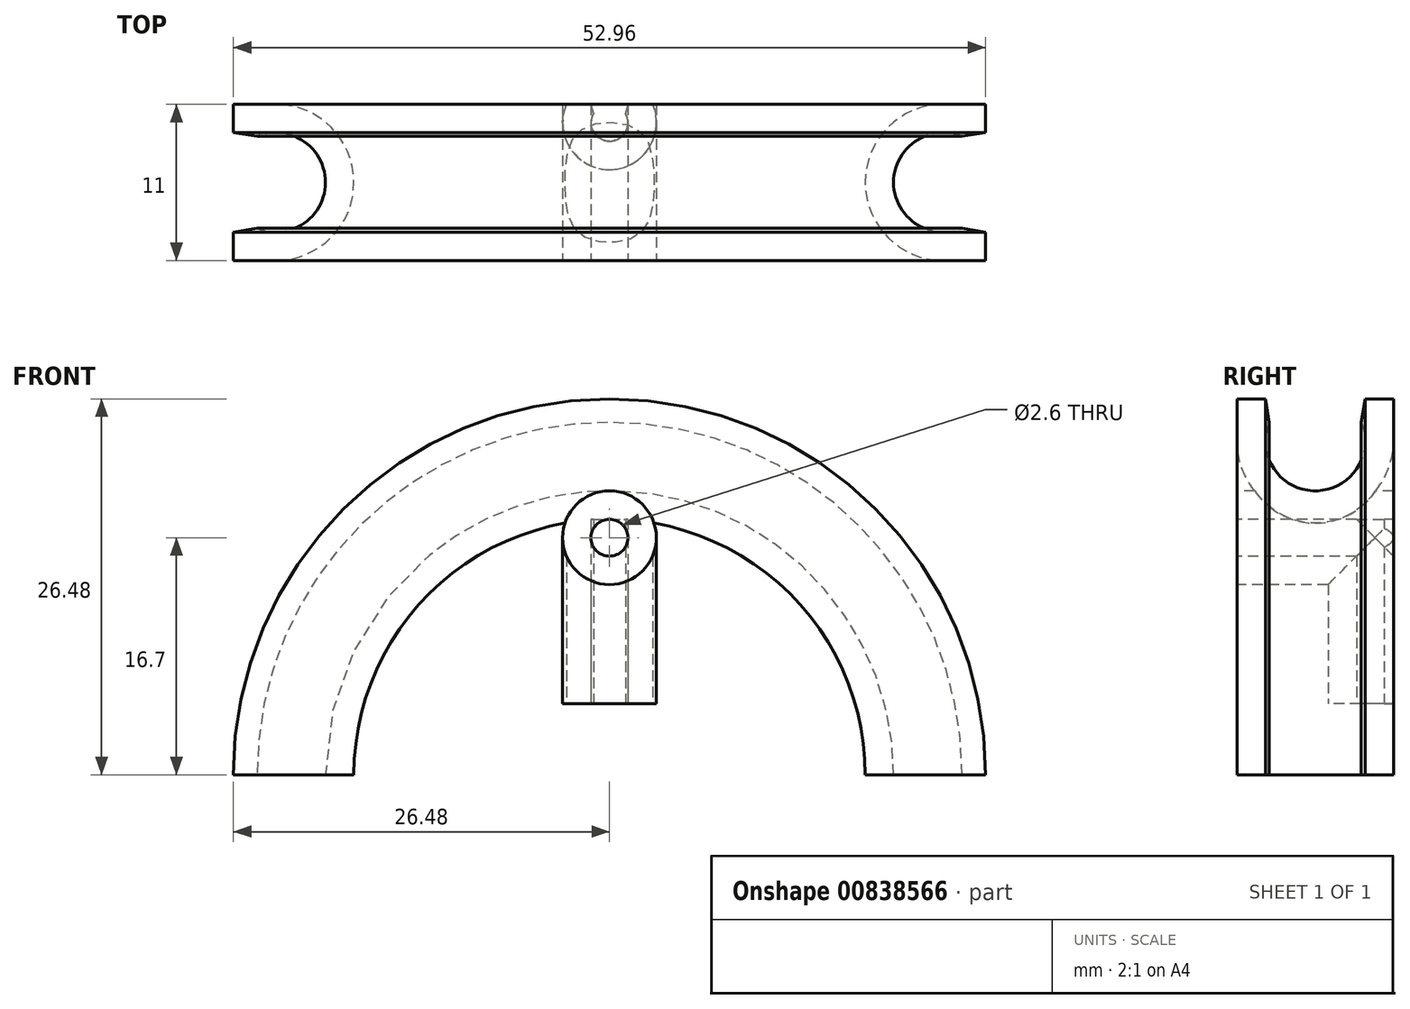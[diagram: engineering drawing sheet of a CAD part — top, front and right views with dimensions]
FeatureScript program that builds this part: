
annotation { "Feature Type Name" : "Feature", "Feature Type Description" : "" }
export const myFeature = defineFeature(function(context is Context, id is Id, definition is map)
    precondition{}
    {
        {
            assignVariable(context, id + "F0", {"name" : "cableDiameter", "lengthValue" : 7 * mm, "variableType" : VariableType.LENGTH});
        }
        {
            assignVariable(context, id + "F1", {"variableType" : VariableType.LENGTH, "name" : "guideRadius", "lengthValue" : 20 * mm});
        }
        {
            assignVariable(context, id + "F2", {"variableType" : VariableType.LENGTH, "name" : "wallThickness", "lengthValue" : 2 * mm});
        }
        {
            assignVariable(context, id + "F3", {"variableType" : VariableType.LENGTH, "name" : "supportDiameter", "lengthValue" : 2.6 * mm});
        }
        {
            assignVariable(context, id + "F4", {"variableType" : VariableType.LENGTH, "name" : "supportWidth", "lengthValue" : 11 * mm});
        }
        {
            var Q0;
            Q0=qCreatedBy(makeId("Front.planeOp"),FACE);
            var sketch = newSketch(context, id + "F5", { "sketchPlane" : qUnion([Q0])});
            skArc(sketch, "E0", {"start": v(20, 0) * mm, "mid": v(0, 20) * mm, "end": v(-20, 0) * mm});
            skSolve(sketch);
        }
        {
            var Q0;
            Q0=qCreatedBy(makeId("Top.planeOp"),FACE);
            var sketch = newSketch(context, id + "F6", { "sketchPlane" : qUnion([Q0])});
            skCircle(sketch, "E1", {"center": v(23.5, 0) * mm, "radius": 3.5 * mm});
            skPoint(sketch, "E2", {"position": v(20, 0) * mm});
            skCircle(sketch, "E3.0", {"center": v(23.5, 0) * mm, "radius": 5.5 * mm});
            skLineSegment(sketch, "E4", {"start": v(23.48, 5.5) * mm, "end": v(23.48, -5.5) * mm, "construction": true});
            skLineSegment(sketch, "E5", {"start": v(23.48, 5.5) * mm, "end": v(26.48, 5.5) * mm});
            skLineSegment(sketch, "E6", {"start": v(26.48, 5.5) * mm, "end": v(26.48, -5.5) * mm});
            skLineSegment(sketch, "E7", {"start": v(26.48, -5.5) * mm, "end": v(23.48, -5.5) * mm});
            skLineSegment(sketch, "E8", {"start": v(23.48, 3.5) * mm, "end": v(26.48, 3.5) * mm, "construction": true});
            skLineSegment(sketch, "E9", {"start": v(23.48, -3.5) * mm, "end": v(26.48, -3.5) * mm, "construction": true});
            skCircle(sketch, "E10", {"center": v(0, 4.2) * mm, "radius": 1.3 * mm});
            skCircle(sketch, "E11.0", {"center": v(0, 4.2) * mm, "radius": 0.9 * mm, "construction": true});
            skCircle(sketch, "E12.0", {"center": v(0, 4.2) * mm, "radius": 3.3 * mm});
            skLineSegment(sketch, "E13", {"start": v(1.3, 4.2) * mm, "end": v(1.3, 7.23) * mm, "construction": true});
            skLineSegment(sketch, "E14", {"start": v(-1.3, 4.2) * mm, "end": v(-1.3, 7.23) * mm, "construction": true});
            skCircle(sketch, "E15.0", {"center": v(23.5, 0) * mm, "radius": 3 * mm, "construction": true});
            skLineSegment(sketch, "E16", {"start": v(26.48, 3.5) * mm, "end": v(24.82, 3.24) * mm});
            skLineSegment(sketch, "E17", {"start": v(26.48, -3.5) * mm, "end": v(24.82, -3.24) * mm});
            skLineSegment(sketch, "E18", {"start": v(0, 0) * mm, "end": v(0, 5.5) * mm, "construction": true});
            skLineSegment(sketch, "E19", {"start": v(23.48, 5.5) * mm, "end": v(-3.03, 5.5) * mm});
            skLineSegment(sketch, "E20", {"start": v(1.3, 5.5) * mm, "end": v(1.12, 4.86) * mm});
            skLineSegment(sketch, "E21", {"start": v(1.12, 4.86) * mm, "end": v(-1.12, 4.86) * mm, "construction": true});
            skLineSegment(sketch, "E22", {"start": v(-1.12, 4.86) * mm, "end": v(-1.3, 5.5) * mm});
            skSolve(sketch);
        }
        {
            var Q0;
            {var subQ6=sQuery(id+"F6.wireOp",EDGE,"E16");Q0=makeQuery(id+"F6.imprint","IMPRINT",FACE,{"disambiguationData":[TD([[makeQuery(id+"F6.imprint","IMPRINT",EDGE,{"derivedFrom":subQ6}),-1.0]])]});}
            var Q1;
            {var subQ0=sQuery(id+"F6.wireOp",EDGE,"E7");Q1=makeQuery(id+"F6.imprint","IMPRINT",FACE,{"disambiguationData":[TD([[makeQuery(id+"F6.imprint","IMPRINT",EDGE,{"derivedFrom":subQ0}),-1.0]])]});}
            var Q2;
            {var subQ0=sQuery(id+"F6.wireOp",EDGE,"E5");Q2=makeQuery(id+"F6.imprint","IMPRINT",FACE,{"disambiguationData":[TD([[makeQuery(id+"F6.imprint","IMPRINT",EDGE,{"derivedFrom":subQ0}),-1.0]])]});}
            var Q3;
            Q3=sQuery(id+"F5.wireOp",EDGE,"E0");
            sweep(context, id + "F7", {"profiles" : qUnion([Q0, Q1, Q2]), "path" : qUnion([Q3])});
        }
        {
            var Q0;
            Q0=qCreatedBy(makeId("Front.planeOp"),FACE);
            var sketch = newSketch(context, id + "F8", { "sketchPlane" : qUnion([Q0])});
            skCircle(sketch, "E23", {"center": v(0, 16.7) * mm, "radius": 1.3 * mm});
            skLineSegment(sketch, "E24", {"start": v(0, 15.4) * mm, "end": v(0, 0) * mm, "construction": true});
            skCircle(sketch, "E25.0", {"center": v(0, 16.7) * mm, "radius": 3.3 * mm});
            skSolve(sketch);
        }
        {
            var Q0;
            Q0=qSketchRegion(id+"F8",true);
            extrude(context, id + "F9", {"entities" : qUnion([Q0]), "operationType" : NewBodyOperationType.ADD, "endBound" : BoundingType.SYMMETRIC, "oppositeDirection" : true, "depth" : getVariable(context, 'supportWidth'), "offsetDistance" : 25 * mm, "hasSecondDirection" : true, "secondDirectionOppositeDirection" : false, "secondDirectionDepth" : getVariable(context, 'cableDiameter') / 2});
        }
        {
            var Q0;
            {var subQ5=sQuery(id+"F6.wireOp",EDGE,"E20");Q0=makeQuery(id+"F6.imprint","IMPRINT",FACE,{"disambiguationData":[TD([[makeQuery(id+"F6.imprint","IMPRINT",EDGE,{"derivedFrom":subQ5}),1.0]])]});}
            extrude(context, id + "F10", {"entities" : qUnion([Q0]), "operationType" : NewBodyOperationType.ADD, "depth" : getVariable(context, 'guideRadius') - getVariable(context, 'wallThickness') - (getVariable(context, 'supportDiameter') / 2), "offsetDistance" : 25 * mm, "hasSecondDirection" : true, "secondDirectionOppositeDirection" : true, "secondDirectionDepth" : -5 * mm});
        }
        {
            var Q0;
            {var subQ0=sQuery(id+"F6.wireOp",EDGE,"E10");var subQ1=makeQuery(id+"F6.imprint","INTERSECT",VERTEX,{"derivedFrom":[subQ0,sQuery(id+"F6.wireOp",EDGE,"E20")]});Q0=makeQuery(id+"F6.imprint","IMPRINT",FACE,{"disambiguationData":[TD([[makeQuery(id+"F6.imprint","IMPRINT",EDGE,{"disambiguationData":[TD([[subQ1,-1.0]])],"derivedFrom":subQ0}),1.0]])]});}
            var Q1;
            {var subQ0=sQuery(id+"F6.wireOp",EDGE,"E20");Q1=makeQuery(id+"F6.imprint","IMPRINT",FACE,{"disambiguationData":[TD([[makeQuery(id+"F6.imprint","IMPRINT",EDGE,{"derivedFrom":subQ0}),-1.0]])]});}
            var Q2;
            {var subQ0=sQuery(id+"F6.wireOp",EDGE,"E22");Q2=makeQuery(id+"F6.imprint","IMPRINT",FACE,{"disambiguationData":[TD([[makeQuery(id+"F6.imprint","IMPRINT",EDGE,{"derivedFrom":subQ0}),-1.0]])]});}
            var Q3;
            {var subQ0=sQuery(id+"F6.wireOp",EDGE,"E19");var subQ4=sQuery(id+"F6.wireOp",EDGE,"E10");var subQ5=makeQuery(id+"F6.imprint","INTERSECT",VERTEX,{"disambiguationData":[OD(0.0)],"derivedFrom":[subQ4,subQ0]});Q3=makeQuery(id+"F6.imprint","IMPRINT",FACE,{"disambiguationData":[TD([[makeQuery(id+"F6.imprint","IMPRINT",EDGE,{"disambiguationData":[TD([[subQ5,-1.0]])],"derivedFrom":subQ4}),-1.0]])]});}
            extrude(context, id + "F11", {"entities" : qUnion([Q0, Q1, Q2, Q3]), "operationType" : NewBodyOperationType.REMOVE, "depth" : getVariable(context, 'guideRadius') - getVariable(context, 'wallThickness'), "offsetDistance" : 25 * mm});
        }
        {
            var Q0;
            Q0=makeQuery(id+"F8.imprint","IMPRINT",FACE,{"disambiguationData":[TD([[makeQuery(id+"F8.imprint","IMPRINT",EDGE,{"derivedFrom":sQuery(id+"F8.wireOp",EDGE,"E23")}),1.0]])]});
            extrude(context, id + "F12", {"entities" : qUnion([Q0]), "operationType" : NewBodyOperationType.REMOVE, "endBound" : BoundingType.SYMMETRIC, "oppositeDirection" : true, "depth" : getVariable(context, 'supportWidth'), "offsetDistance" : 25 * mm});
        }
    });
